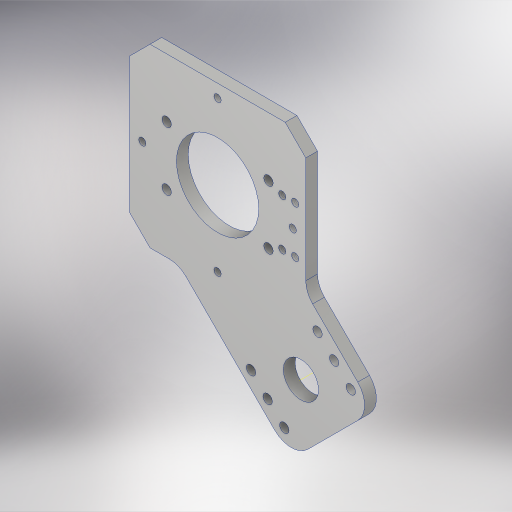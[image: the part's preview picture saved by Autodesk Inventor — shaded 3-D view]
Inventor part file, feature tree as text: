
AUTODESK INVENTOR PART (.ipt)
format: ipt  version: 2023.4 (Build 274418000, 418)  size: 470,528 bytes
history: native  units: in
note: dims shown in document units (in); Inventor stores cm internally (conversion verified against a paired STEP export)
features: sketch x7, hole x5, extrude x4, projected_geometry x3, fillet x2, other x1
ambient origin geometry x8: Origin, YZ Plane, XZ Plane, XY Plane, X Axis, Y Axis, Z Axis, Center Point
bodies: Solid1 (feature_tree)
feature tree (22):
  extrude  "Extrusion1"  Depth=4.7244in
  hole  "Hole1"  [1 undecoded]
  hole  "Hole2"  [1 undecoded]
  extrude  "Extrusion2"  TaperAngle=0.0deg  [1 undecoded]
  sketch  "Sketch5"  dims[d22=0.201in d23=0.38in d24=0.563in d25=0.12in d26=0.5635in d27=1.0in d28=0.8108in d29=0.5in]
  extrude  "Extrusion3"  Depth=1.4173in
  hole  "Hole3"  [1 undecoded]
  other  "Work Axis1"
  fillet  "Fillet2"  Radius=2.0in
  extrude  "Extrusion5"  Depth=0.5in
  hole  "Hole4"  [1 undecoded]
  hole  "Hole5"  [1 undecoded]
  fillet  "Fillet3"  Radius=0.3937in
  sketch  "Sketch2"  dims[d3=0.0in d5=4.7244in]
  sketch  "Sketch3"  dims[d10=0.156in d11=0.38in d12=0.563in d13=0.12in d14=0.5635in d15=1.0in d16=0.8108in d17=2.5in]
  sketch  "Sketch4"  dims[d18=2.3622in d20=360.0deg]
  sketch  "Sketch7"  dims[d30=1.75in d31=0.0in d32=0.0in]
  projected_geometry  "Projected Loop2"
  sketch  "Sketch8"  dims[d33=5.0394in d34=1.4173in]
  projected_geometry  "Projected Loop3"
  sketch  "Sketch9"  dims[d35=3.7725in d36=3.7725in d37=2.0in d38=0.5in d39=0.5in d40=1.1811in d42=0.5in d43=0.3937in d45=1.0in d47=45.0deg d48=2.0in d49=0.25in d50=0.9587in d51=0.25in d53=1.0in d54=0.0in d55=0.75in d56=0.201in d57=0.75in d58=0.563in d59=0.12in d60=0.5635in d61=1.0in d62=0.8108in d63=0.5in d64=45.0deg d68=4.7244in d69=0.0in d70=0.0in d71=0.26in d73=2.7559in d74=3.2in d75=1.5748in d77=360.0deg d79=1.0in d80=0.5in d81=0.156in d82=0.38in d83=0.375in d84=0.25in d85=0.5635in d86=1.0in d87=0.8108in d88=1.375in d89=1.75in d90=0.225in d91=0.201in d92=0.156in d93=0.38in d94=0.385in d95=0.25in d96=0.5635in d97=1.0in d98=0.8108in]
  projected_geometry  "Project Cut Edges1"
note: 6 required parameter values undecoded (feature->parameter linkage not recoverable at this tier; creation-order binding heuristic only, values carry confidence <= 0.55)
